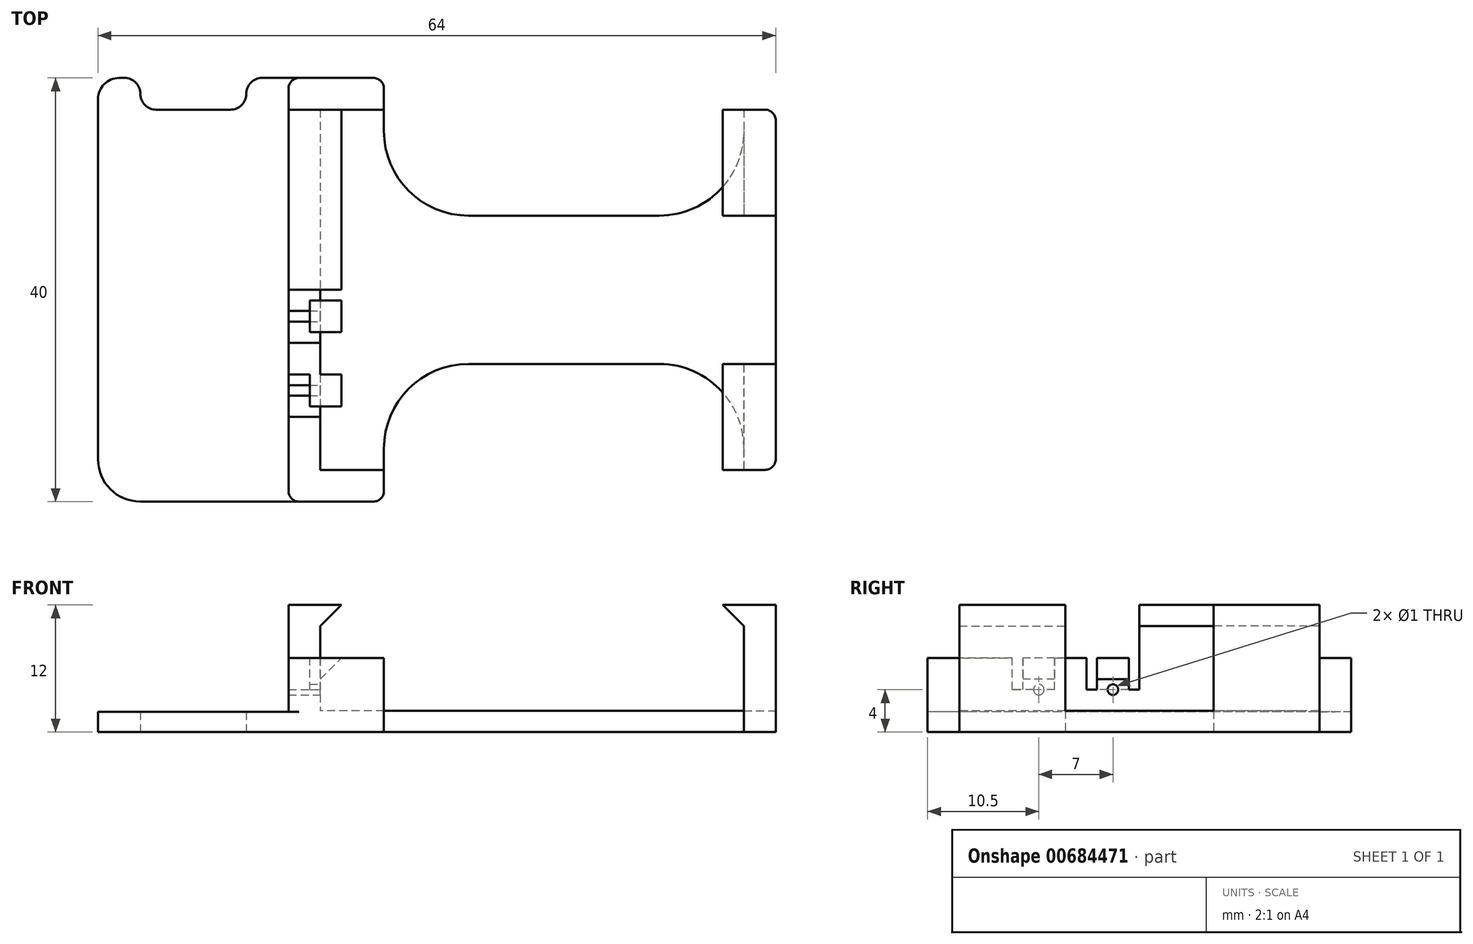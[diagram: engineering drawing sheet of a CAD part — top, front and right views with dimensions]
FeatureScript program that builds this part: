
annotation { "Feature Type Name" : "Feature", "Feature Type Description" : "" }
export const myFeature = defineFeature(function(context is Context, id is Id, definition is map)
    precondition{}
    {
        {
            var Q0;
            Q0=qCreatedBy(makeId("Top.planeOp"),FACE);
            var sketch = newSketch(context, id + "F0", { "sketchPlane" : qUnion([Q0])});
            skLineSegment(sketch, "E0.bottom", {"start": v(20, 17) * mm, "end": v(-20, 17) * mm});
            skLineSegment(sketch, "E0.top", {"start": v(20, -17) * mm, "end": v(-20, -17) * mm});
            skLineSegment(sketch, "E0.left", {"start": v(20, 17) * mm, "end": v(20, -15) * mm});
            skLineSegment(sketch, "E0.right", {"start": v(-20, 17) * mm, "end": v(-20, -17) * mm});
            skPoint(sketch, "E0.middle", {"position": v(0, 0) * mm});
            skLineSegment(sketch, "E1.bottom", {"start": v(20, 17) * mm, "end": v(22, 17) * mm});
            skLineSegment(sketch, "E1.top", {"start": v(20, -17) * mm, "end": v(22, -17) * mm});
            skLineSegment(sketch, "E1.left", {"start": v(20, -15) * mm, "end": v(20, -17) * mm});
            skLineSegment(sketch, "E1.right", {"start": v(23, 16) * mm, "end": v(23, -16) * mm});
            skLineSegment(sketch, "E2.bottom", {"start": v(-20, -17) * mm, "end": v(-23, -17) * mm});
            skLineSegment(sketch, "E2.top", {"start": v(-20, 17) * mm, "end": v(-23, 17) * mm});
            skLineSegment(sketch, "E2.left", {"start": v(-20, -17) * mm, "end": v(-20, -15) * mm});
            skLineSegment(sketch, "E2.right", {"start": v(-23, -17) * mm, "end": v(-23, 17) * mm});
            skLineSegment(sketch, "E3", {"start": v(-12, 7) * mm, "end": v(12, 7) * mm});
            skLineSegment(sketch, "E4", {"start": v(-12, -7) * mm, "end": v(12, -7) * mm});
            skArc(sketch, "E5.filletArc", {"start": v(20, -15) * mm, "mid": v(17.66, -9.34) * mm, "end": v(12, -7) * mm});
            skPoint(sketch, "E6.newPointA", {"position": v(20, -17) * mm});
            skArc(sketch, "E6.filletArc", {"start": v(12, 7) * mm, "mid": v(17.66, 9.34) * mm, "end": v(20, 15) * mm});
            skLineSegment(sketch, "E7", {"start": v(-23, -17) * mm, "end": v(-23, -19) * mm});
            skLineSegment(sketch, "E8", {"start": v(-22, -20) * mm, "end": v(-15, -20) * mm});
            skLineSegment(sketch, "E9", {"start": v(-14, -19) * mm, "end": v(-14, -18) * mm});
            skLineSegment(sketch, "E10", {"start": v(-15, -17) * mm, "end": v(-20, -17) * mm});
            skPoint(sketch, "E11.visualSharp", {"position": v(-14, -20) * mm});
            skArc(sketch, "E11.filletArc", {"start": v(-15, -20) * mm, "mid": v(-14.3, -19.7) * mm, "end": v(-14, -19) * mm});
            skPoint(sketch, "E12.visualSharp", {"position": v(-23, -20) * mm});
            skArc(sketch, "E12.filletArc", {"start": v(-23, -19) * mm, "mid": v(-22.7, -19.7) * mm, "end": v(-22, -20) * mm});
            skLineSegment(sketch, "E13", {"start": v(-23, 17) * mm, "end": v(-23, 19) * mm});
            skLineSegment(sketch, "E14", {"start": v(-22, 20) * mm, "end": v(-15, 20) * mm});
            skLineSegment(sketch, "E15", {"start": v(-14, 19) * mm, "end": v(-14, 18) * mm});
            skLineSegment(sketch, "E16", {"start": v(-15, 17) * mm, "end": v(-23, 17) * mm});
            skPoint(sketch, "E17.visualSharp", {"position": v(-14, 20) * mm});
            skArc(sketch, "E17.filletArc", {"start": v(-14, 19) * mm, "mid": v(-14.3, 19.7) * mm, "end": v(-15, 20) * mm});
            skPoint(sketch, "E18.visualSharp", {"position": v(-23, 20) * mm});
            skArc(sketch, "E18.filletArc", {"start": v(-22, 20) * mm, "mid": v(-22.7, 19.7) * mm, "end": v(-23, 19) * mm});
            skPoint(sketch, "E19.visualSharp", {"position": v(23, 17) * mm});
            skArc(sketch, "E19.filletArc", {"start": v(23, 16) * mm, "mid": v(22.7, 16.7) * mm, "end": v(22, 17) * mm});
            skPoint(sketch, "E20.visualSharp", {"position": v(23, -17) * mm});
            skArc(sketch, "E20.filletArc", {"start": v(22, -17) * mm, "mid": v(22.7, -16.7) * mm, "end": v(23, -16) * mm});
            skPoint(sketch, "E21.visualSharp", {"position": v(-14, -17) * mm});
            skPoint(sketch, "E22.visualSharp", {"position": v(-14, 17) * mm});
            skLineSegment(sketch, "E23", {"start": v(-14, -18) * mm, "end": v(-14, -15) * mm});
            skLineSegment(sketch, "E24", {"start": v(-6, -7) * mm, "end": v(-12, -7) * mm});
            skLineSegment(sketch, "E25", {"start": v(-6, 7) * mm, "end": v(-12, 7) * mm});
            skArc(sketch, "E26.filletArc", {"start": v(-6, -7) * mm, "mid": v(-11.66, -9.34) * mm, "end": v(-14, -15) * mm});
            skLineSegment(sketch, "E27", {"start": v(-14, 15) * mm, "end": v(-14, 18) * mm});
            skPoint(sketch, "E28.visualSharp", {"position": v(-14, 7) * mm});
            skArc(sketch, "E28.filletArc", {"start": v(-14, 15) * mm, "mid": v(-11.66, 9.34) * mm, "end": v(-6, 7) * mm});
            skSolve(sketch);
        }
        {
            var Q0;
            Q0=makeQuery(id+"F0.imprint","IMPRINT",FACE,{"disambiguationData":[TD([[makeQuery(id+"F0.imprint","IMPRINT",EDGE,{"derivedFrom":sQuery(id+"F0.wireOp",EDGE,"E3")}),-1.0]])]});
            var Q1;
            Q1=makeQuery(id+"F0.imprint","IMPRINT",FACE,{"disambiguationData":[TD([[makeQuery(id+"F0.imprint","IMPRINT",EDGE,{"derivedFrom":sQuery(id+"F0.wireOp",EDGE,"E2.bottom")}),-1.0]])]});
            var Q2;
            {var subQ0=sQuery(id+"F0.wireOp",EDGE,"E1.bottom");Q2=makeQuery(id+"F0.imprint","IMPRINT",FACE,{"disambiguationData":[TD([[makeQuery(id+"F0.imprint","IMPRINT",EDGE,{"derivedFrom":subQ0}),-1.0]])]});}
            extrude(context, id + "F1", {"entities" : qUnion([Q0, Q1, Q2]), "depth" : 2 * mm, "offsetDistance" : 25 * mm});
        }
        {
            var Q0;
            Q0=makeQuery(id+"F1.opExtrude","CAP_FACE",FACE,{"disambiguationData":[OSD([sQuery(id+"F0.wireOp",EDGE,"E0.left"),sQuery(id+"F0.wireOp",EDGE,"E0.right"),sQuery(id+"F0.wireOp",EDGE,"E1.bottom"),sQuery(id+"F0.wireOp",EDGE,"E1.top"),sQuery(id+"F0.wireOp",EDGE,"E1.left"),sQuery(id+"F0.wireOp",EDGE,"E1.right"),sQuery(id+"F0.wireOp",EDGE,"E2.bottom"),sQuery(id+"F0.wireOp",EDGE,"E2.top"),sQuery(id+"F0.wireOp",EDGE,"E2.left"),sQuery(id+"F0.wireOp",EDGE,"E2.right"),sQuery(id+"F0.wireOp",EDGE,"E3"),sQuery(id+"F0.wireOp",EDGE,"E4"),sQuery(id+"F0.wireOp",EDGE,"0d2e5045-32be-4d61-923d-7fe529c6475d.filletArc"),sQuery(id+"F0.wireOp",EDGE,"E5.filletArc"),sQuery(id+"F0.wireOp",EDGE,"E6.filletArc"),sQuery(id+"F0.wireOp",EDGE,"e1b89db7-bc73-4bd3-85a6-a36b4de26723.filletArc")])],"isStart":false});
            var sketch = newSketch(context, id + "F2", { "sketchPlane" : qUnion([Q0])});
            skArc(sketch, "E29.0.0", {"start": v(12, -7) * mm, "mid": v(17.66, -9.34) * mm, "end": v(20, -15) * mm});
            skLineSegment(sketch, "E29.0.1", {"start": v(20, -15) * mm, "end": v(20, -17) * mm});
            skLineSegment(sketch, "E29.0.2", {"start": v(20, -17) * mm, "end": v(22, -17) * mm});
            skLineSegment(sketch, "E29.0.3", {"start": v(23, -17) * mm, "end": v(23, 16) * mm});
            skLineSegment(sketch, "E29.0.4", {"start": v(23, 17) * mm, "end": v(20, 17) * mm});
            skLineSegment(sketch, "E29.0.5", {"start": v(20, 15) * mm, "end": v(20, -17) * mm});
            skArc(sketch, "E29.0.6", {"start": v(20, 15) * mm, "mid": v(17.66, 9.34) * mm, "end": v(12, 7) * mm});
            skLineSegment(sketch, "E29.0.7", {"start": v(12, 7) * mm, "end": v(-6, 7) * mm});
            skArc(sketch, "E29.0.8", {"start": v(-6, 7) * mm, "mid": v(-11.66, 9.34) * mm, "end": v(-14, 15) * mm});
            skLineSegment(sketch, "E29.0.10", {"start": v(-14, 17) * mm, "end": v(-23, 17) * mm});
            skLineSegment(sketch, "E29.0.11", {"start": v(-23, 17) * mm, "end": v(-23, -17) * mm});
            skLineSegment(sketch, "E29.0.12", {"start": v(-23, -17) * mm, "end": v(-14, -17) * mm});
            skLineSegment(sketch, "E29.0.13", {"start": v(-14, -17) * mm, "end": v(-14, -15) * mm});
            skLineSegment(sketch, "E29.0.15", {"start": v(-12, -7) * mm, "end": v(12, -7) * mm});
            skLineSegment(sketch, "E30", {"start": v(20, -7) * mm, "end": v(23, -7) * mm});
            skLineSegment(sketch, "E31", {"start": v(20, 7) * mm, "end": v(23, 7) * mm});
            skLineSegment(sketch, "E32", {"start": v(-14, -7) * mm, "end": v(-23, -7) * mm});
            skLineSegment(sketch, "E33", {"start": v(-23, 0) * mm, "end": v(-14, 0) * mm});
            skLineSegment(sketch, "E34", {"start": v(-20, 17) * mm, "end": v(-20, -17) * mm});
            skSolve(sketch);
        }
        {
            var Q0;
            {var subQ1=sQuery(id+"F2.wireOp",EDGE,"E29.0.10");Q0=makeQuery(id+"F2.imprint","IMPRINT",FACE,{"disambiguationData":[TD([[makeQuery(id+"F2.imprint","IMPRINT",EDGE,{"derivedFrom":subQ1}),1.0]])]});}
            var Q1;
            {var subQ3=sQuery(id+"F2.wireOp",EDGE,"E29.0.2");Q1=makeQuery(id+"F2.imprint","IMPRINT",FACE,{"disambiguationData":[TD([[makeQuery(id+"F2.imprint","IMPRINT",EDGE,{"derivedFrom":subQ3}),1.0]])]});}
            var Q2;
            {var subQ3=sQuery(id+"F2.wireOp",EDGE,"E29.0.4");Q2=makeQuery(id+"F2.imprint","IMPRINT",FACE,{"disambiguationData":[TD([[makeQuery(id+"F2.imprint","IMPRINT",EDGE,{"derivedFrom":subQ3}),-1.0]])]});}
            var Q3;
            {var subQ0=sQuery(id+"F2.wireOp",EDGE,"SwYouN3J-6pRH-B4eC-V0e7-ENGrIOtCNmfV");Q3=makeQuery(id+"F2.imprint","IMPRINT",FACE,{"disambiguationData":[TD([[makeQuery(id+"F2.imprint","IMPRINT",EDGE,{"derivedFrom":subQ0}),1.0]])]});}
            extrude(context, id + "F3", {"entities" : qUnion([Q0, Q1, Q2, Q3]), "operationType" : NewBodyOperationType.ADD, "depth" : 10 * mm, "offsetDistance" : 25 * mm});
        }
        {
            var Q0;
            Q0=makeQuery(id+"F3.boolean.opBoolean","MERGE",FACE,{"derivedFrom":[makeQuery(id+"F1.opExtrude","SWEPT_FACE",FACE,{"disambiguationData":[OSD([sQuery(id+"F0.wireOp",EDGE,"E1.left")])]}),makeQuery(id+"F3.opExtrude","SWEPT_FACE",FACE,{"disambiguationData":[OSD([sQuery(id+"F2.wireOp",EDGE,"E29.0.5")])]})]});
            var sketch = newSketch(context, id + "F4", { "sketchPlane" : qUnion([Q0])});
            skLineSegment(sketch, "E35.bottom", {"start": v(-17, 12) * mm, "end": v(-7, 12) * mm});
            skLineSegment(sketch, "E35.top", {"start": v(-17, 10) * mm, "end": v(-7, 10) * mm});
            skLineSegment(sketch, "E35.left", {"start": v(-17, 12) * mm, "end": v(-17, 10) * mm});
            skLineSegment(sketch, "E35.right", {"start": v(-7, 12) * mm, "end": v(-7, 10) * mm});
            skLineSegment(sketch, "E36.0.0", {"start": v(15, 0) * mm, "end": v(17, 0) * mm});
            skLineSegment(sketch, "E36.0.1", {"start": v(17, 0) * mm, "end": v(17, 12) * mm});
            skLineSegment(sketch, "E36.0.2", {"start": v(17, 12) * mm, "end": v(7, 12) * mm});
            skLineSegment(sketch, "E36.0.3", {"start": v(7, 12) * mm, "end": v(7, 2) * mm});
            skLineSegment(sketch, "E36.0.4", {"start": v(7, 2) * mm, "end": v(15, 2) * mm});
            skLineSegment(sketch, "E36.0.5", {"start": v(15, 2) * mm, "end": v(15, 0) * mm});
            skLineSegment(sketch, "E37.0.0", {"start": v(-15, 0) * mm, "end": v(-17, 0) * mm});
            skLineSegment(sketch, "E37.0.1", {"start": v(-17, 0) * mm, "end": v(-17, 12) * mm});
            skLineSegment(sketch, "E37.0.2", {"start": v(-17, 12) * mm, "end": v(17, 12) * mm});
            skLineSegment(sketch, "E37.0.3", {"start": v(17, 12) * mm, "end": v(17, 0) * mm});
            skLineSegment(sketch, "E37.0.4", {"start": v(17, 0) * mm, "end": v(15, 0) * mm});
            skLineSegment(sketch, "E37.0.5", {"start": v(15, 0) * mm, "end": v(15, 2) * mm});
            skLineSegment(sketch, "E37.0.6", {"start": v(15, 2) * mm, "end": v(-15, 2) * mm});
            skLineSegment(sketch, "E37.0.7", {"start": v(-15, 2) * mm, "end": v(-15, 0) * mm});
            skLineSegment(sketch, "E38.top", {"start": v(17, 10) * mm, "end": v(7, 10) * mm});
            skLineSegment(sketch, "E38.left", {"start": v(17, 12) * mm, "end": v(17, 10) * mm});
            skLineSegment(sketch, "E38.right", {"start": v(7, 12) * mm, "end": v(7, 10) * mm});
            skSolve(sketch);
        }
        {
            var Q0;
            {var subQ0=sQuery(id+"F4.wireOp",EDGE,"E35.top");Q0=makeQuery(id+"F4.imprint","IMPRINT",FACE,{"disambiguationData":[TD([[makeQuery(id+"F4.imprint","IMPRINT",EDGE,{"derivedFrom":subQ0}),1.0]])]});}
            var Q1;
            Q1=makeQuery(id+"F4.imprint","IMPRINT",FACE,{"disambiguationData":[TD([[makeQuery(id+"F4.imprint","IMPRINT",EDGE,{"derivedFrom":sQuery(id+"F4.wireOp",EDGE,"E36.0.2")}),-1.0]])]});
            extrude(context, id + "F5", {"entities" : qUnion([Q0, Q1]), "operationType" : NewBodyOperationType.ADD, "depth" : 2 * mm, "offsetDistance" : 25 * mm});
        }
        {
            var Q0;
            Q0=makeQuery(id+"F5.opExtrude","CAP_EDGE",EDGE,{"disambiguationData":[OSD([sQuery(id+"F4.wireOp",EDGE,"E35.top")])],"isStart":false});
            var Q1;
            Q1=makeQuery(id+"F5.opExtrude","CAP_EDGE",EDGE,{"disambiguationData":[OSD([sQuery(id+"F4.wireOp",EDGE,"E38.top")])],"isStart":false});
            chamfer(context, id + "F6", {"entities" : qUnion([Q0, Q1]), "width" : 2 * mm, "tangentPropagation" : true});
        }
        {
            var Q0;
            {var subQ0=sQuery(id+"F2.wireOp",EDGE,"E29.0.12");Q0=makeQuery(id+"F2.imprint","IMPRINT",FACE,{"disambiguationData":[TD([[makeQuery(id+"F2.imprint","IMPRINT",EDGE,{"derivedFrom":subQ0}),-1.0]])]});}
            var Q1;
            {var subQ0=sQuery(id+"F2.wireOp",EDGE,"E32");Q1=makeQuery(id+"F2.imprint","IMPRINT",FACE,{"disambiguationData":[TD([[makeQuery(id+"F2.imprint","IMPRINT",EDGE,{"derivedFrom":subQ0}),-1.0]])]});}
            extrude(context, id + "F7", {"entities" : qUnion([Q0, Q1]), "operationType" : NewBodyOperationType.ADD, "depth" : 5 * mm, "offsetDistance" : 25 * mm});
        }
        {
            var Q0;
            Q0=makeQuery(id+"F0.imprint","IMPRINT",FACE,{"disambiguationData":[TD([[makeQuery(id+"F0.imprint","IMPRINT",EDGE,{"derivedFrom":sQuery(id+"F0.wireOp",EDGE,"E2.bottom")}),1.0]])]});
            var Q1;
            {var subQ3=sQuery(id+"F0.wireOp",EDGE,"E13");Q1=makeQuery(id+"F0.imprint","IMPRINT",FACE,{"disambiguationData":[TD([[makeQuery(id+"F0.imprint","IMPRINT",EDGE,{"derivedFrom":subQ3}),-1.0]])]});}
            extrude(context, id + "F8", {"entities" : qUnion([Q0, Q1]), "operationType" : NewBodyOperationType.ADD, "depth" : 7 * mm, "offsetDistance" : 25 * mm});
        }
        {
            var Q0;
            {var subQ0=sQuery(id+"F2.wireOp",EDGE,"E34");Q0=makeQuery(id+"F7.boolean.opBoolean","MERGE",FACE,{"derivedFrom":[makeQuery(id+"F3.opExtrude","SWEPT_FACE",FACE,{"disambiguationData":[OSD([subQ0])]}),makeQuery(id+"F7.opExtrude","SWEPT_FACE",FACE,{"disambiguationData":[OSD([subQ0])]})]});}
            var sketch = newSketch(context, id + "F9", { "sketchPlane" : qUnion([Q0])});
            skLineSegment(sketch, "E39.bottom", {"start": v(17, 12) * mm, "end": v(0, 12) * mm});
            skLineSegment(sketch, "E39.top", {"start": v(17, 10) * mm, "end": v(0, 10) * mm});
            skLineSegment(sketch, "E39.left", {"start": v(17, 12) * mm, "end": v(17, 10) * mm});
            skLineSegment(sketch, "E39.right", {"start": v(0, 12) * mm, "end": v(0, 10) * mm});
            skSolve(sketch);
        }
        {
            var Q0;
            Q0=makeQuery(id+"F9.imprint","IMPRINT",FACE,{"disambiguationData":[TD([[makeQuery(id+"F9.imprint","IMPRINT",EDGE,{"derivedFrom":sQuery(id+"F9.wireOp",EDGE,"E39.bottom")}),1.0]])]});
            extrude(context, id + "F10", {"entities" : qUnion([Q0]), "operationType" : NewBodyOperationType.ADD, "depth" : 2 * mm, "offsetDistance" : 25 * mm});
        }
        {
            var Q0;
            Q0=makeQuery(id+"F10.opExtrude","CAP_EDGE",EDGE,{"disambiguationData":[OSD([sQuery(id+"F9.wireOp",EDGE,"E39.top")])],"isStart":false});
            chamfer(context, id + "F11", {"entities" : qUnion([Q0]), "width" : 2 * mm, "tangentPropagation" : true});
        }
        {
            var Q0;
            Q0=makeQuery(id+"F8.boolean.opBoolean","MERGE",FACE,{"derivedFrom":[makeQuery(id+"F7.opExtrude","CAP_FACE",FACE,{"disambiguationData":[OSD([sQuery(id+"F2.wireOp",EDGE,"E29.0.11"),sQuery(id+"F2.wireOp",EDGE,"E29.0.12"),sQuery(id+"F2.wireOp",EDGE,"E33"),sQuery(id+"F2.wireOp",EDGE,"E34")])],"isStart":false}),makeQuery(id+"F8.opExtrude","CAP_FACE",FACE,{"disambiguationData":[OSD([sQuery(id+"F0.wireOp",EDGE,"E0.top"),sQuery(id+"F0.wireOp",EDGE,"E2.bottom"),sQuery(id+"F0.wireOp",EDGE,"E7"),sQuery(id+"F0.wireOp",EDGE,"E8"),sQuery(id+"F0.wireOp",EDGE,"E9"),sQuery(id+"F0.wireOp",EDGE,"E10"),sQuery(id+"F0.wireOp",EDGE,"E11.filletArc"),sQuery(id+"F0.wireOp",EDGE,"E12.filletArc"),sQuery(id+"F0.wireOp",EDGE,"E23")])],"isStart":false})]});
            var sketch = newSketch(context, id + "F12", { "sketchPlane" : qUnion([Q0])});
            skLineSegment(sketch, "E40", {"start": v(-20, -17) * mm, "end": v(-20, -9.5) * mm});
            skLineSegment(sketch, "E41", {"start": v(-20, -9.5) * mm, "end": v(-19.15, -9.5) * mm});
            skLineSegment(sketch, "E42", {"start": v(-20, -2.5) * mm, "end": v(-17.2, -2.5) * mm});
            skLineSegment(sketch, "E43.bottom", {"start": v(-23, -8) * mm, "end": v(-17, -8) * mm});
            skLineSegment(sketch, "E43.top", {"start": v(-23, -11) * mm, "end": v(-17, -11) * mm});
            skLineSegment(sketch, "E43.left", {"start": v(-23, -8) * mm, "end": v(-23, -11) * mm});
            skLineSegment(sketch, "E43.right", {"start": v(-17, -8) * mm, "end": v(-17, -11) * mm});
            skPoint(sketch, "E43.middle", {"position": v(-20, -9.5) * mm});
            skLineSegment(sketch, "E44.bottom", {"start": v(-23, -1) * mm, "end": v(-17, -1) * mm});
            skLineSegment(sketch, "E44.top", {"start": v(-23, -4) * mm, "end": v(-17, -4) * mm});
            skLineSegment(sketch, "E44.left", {"start": v(-23, -1) * mm, "end": v(-23, -4) * mm});
            skLineSegment(sketch, "E44.right", {"start": v(-17, -1) * mm, "end": v(-17, -4) * mm});
            skPoint(sketch, "E44.middle", {"position": v(-20, -2.5) * mm});
            skSolve(sketch);
        }
        {
            var Q0;
            {var subQ0=sQuery(id+"F2.wireOp",EDGE,"E34");Q0=makeQuery(id+"F7.boolean.opBoolean","MERGE",FACE,{"derivedFrom":[makeQuery(id+"F3.opExtrude","SWEPT_FACE",FACE,{"disambiguationData":[OSD([subQ0])]}),makeQuery(id+"F7.opExtrude","SWEPT_FACE",FACE,{"disambiguationData":[OSD([subQ0])]})]});}
            var sketch = newSketch(context, id + "F13", { "sketchPlane" : qUnion([Q0])});
            skLineSegment(sketch, "E45", {"start": v(-17, 7) * mm, "end": v(-9.5, 7) * mm});
            skLineSegment(sketch, "E46", {"start": v(-9.5, 7) * mm, "end": v(-9.5, 6) * mm});
            skLineSegment(sketch, "E47", {"start": v(-2.5, 7) * mm, "end": v(-2.5, 6) * mm});
            skLineSegment(sketch, "E48.bottom", {"start": v(-8, 7) * mm, "end": v(-11, 7) * mm});
            skLineSegment(sketch, "E48.top", {"start": v(-8, 5) * mm, "end": v(-11, 5) * mm});
            skLineSegment(sketch, "E48.left", {"start": v(-8, 7) * mm, "end": v(-8, 5) * mm});
            skLineSegment(sketch, "E48.right", {"start": v(-11, 7) * mm, "end": v(-11, 5) * mm});
            skPoint(sketch, "E48.middle", {"position": v(-9.5, 6) * mm});
            skLineSegment(sketch, "E49.bottom", {"start": v(-1, 7) * mm, "end": v(-4, 7) * mm});
            skLineSegment(sketch, "E49.top", {"start": v(-1, 5) * mm, "end": v(-4, 5) * mm});
            skLineSegment(sketch, "E49.left", {"start": v(-1, 7) * mm, "end": v(-1, 5) * mm});
            skLineSegment(sketch, "E49.right", {"start": v(-4, 7) * mm, "end": v(-4, 5) * mm});
            skPoint(sketch, "E49.middle", {"position": v(-2.5, 6) * mm});
            skSolve(sketch);
        }
        {
            var Q0;
            Q0 = qSketchRegion(id + "F13", true);
            extrude(context, id + "F14", {"entities" : qUnion([Q0]), "operationType" : NewBodyOperationType.ADD, "depth" : 2 * mm, "offsetDistance" : 25 * mm});
        }
        {
            var Q0;
            Q0=makeQuery(id+"F14.opExtrude","CAP_EDGE",EDGE,{"disambiguationData":[OSD([sQuery(id+"F13.wireOp",EDGE,"E48.top")])],"isStart":false});
            var Q1;
            Q1=makeQuery(id+"F14.opExtrude","CAP_EDGE",EDGE,{"disambiguationData":[OSD([sQuery(id+"F13.wireOp",EDGE,"E49.top")])],"isStart":false});
            chamfer(context, id + "F15", {"entities" : qUnion([Q0, Q1]), "width" : 2 * mm, "tangentPropagation" : true});
        }
        {
            var Q0;
            {var subQ0=sQuery(id+"F12.wireOp",EDGE,"E43.bottom");var subQ3=makeQuery(id+"F7.opExtrude","CAP_EDGE",EDGE,{"disambiguationData":[OSD([sQuery(id+"F2.wireOp",EDGE,"E34")])],"isStart":false});var subQ4=makeQuery(id+"F12.imprint","INTERSECT",VERTEX,{"derivedFrom":[subQ3,subQ0]});Q0=makeQuery(id+"F12.imprint","IMPRINT",FACE,{"disambiguationData":[TD([[makeQuery(id+"F12.imprint","IMPRINT",EDGE,{"disambiguationData":[TD([[subQ4,1.0]])],"derivedFrom":subQ3}),-1.0]])]});}
            var sketch = newSketch(context, id + "F16", { "sketchPlane" : qUnion([Q0])});
            skLineSegment(sketch, "E50.0.0", {"start": v(-23, -1) * mm, "end": v(-23, -4) * mm});
            skLineSegment(sketch, "E50.0.1", {"start": v(-21, -4) * mm, "end": v(-20, -4) * mm});
            skLineSegment(sketch, "E50.0.2", {"start": v(-20, -4) * mm, "end": v(-20, -2.5) * mm});
            skLineSegment(sketch, "E50.0.3", {"start": v(-20, -2.5) * mm, "end": v(-20, -1) * mm});
            skLineSegment(sketch, "E50.0.4", {"start": v(-20, -1) * mm, "end": v(-21, -1) * mm});
            skLineSegment(sketch, "E51.0.0", {"start": v(-23, -8) * mm, "end": v(-23, -11) * mm});
            skLineSegment(sketch, "E51.0.1", {"start": v(-21, -11) * mm, "end": v(-20, -11) * mm});
            skLineSegment(sketch, "E51.0.2", {"start": v(-20, -11) * mm, "end": v(-20, -9.5) * mm});
            skLineSegment(sketch, "E51.0.3", {"start": v(-20, -9.5) * mm, "end": v(-20, -8) * mm});
            skLineSegment(sketch, "E51.0.4", {"start": v(-20, -8) * mm, "end": v(-21, -8) * mm});
            skLineSegment(sketch, "E52", {"start": v(-21, -1) * mm, "end": v(-21, -4) * mm});
            skLineSegment(sketch, "E53", {"start": v(-21, -8) * mm, "end": v(-21, -11) * mm});
            skLineSegment(sketch, "E54.0", {"start": v(-20, -17) * mm, "end": v(-20, -9.5) * mm});
            skLineSegment(sketch, "E55.0", {"start": v(-20, -4) * mm, "end": v(-20, -8) * mm});
            skLineSegment(sketch, "E56.0", {"start": v(-20, 0) * mm, "end": v(-20, -1) * mm});
            skLineSegment(sketch, "E57", {"start": v(-20, -12) * mm, "end": v(-21, -12) * mm});
            skLineSegment(sketch, "E58", {"start": v(-21, -7) * mm, "end": v(-20, -7) * mm});
            skLineSegment(sketch, "E59", {"start": v(-21, -7) * mm, "end": v(-23, -7) * mm});
            skLineSegment(sketch, "E60", {"start": v(-23, -7) * mm, "end": v(-23, -8) * mm});
            skLineSegment(sketch, "E61", {"start": v(-23, -11) * mm, "end": v(-23, -12) * mm});
            skLineSegment(sketch, "E62", {"start": v(-23, -12) * mm, "end": v(-21, -12) * mm});
            skLineSegment(sketch, "E63", {"start": v(-20, -5) * mm, "end": v(-23, -5) * mm});
            skLineSegment(sketch, "E64", {"start": v(-23, -5) * mm, "end": v(-23, -4) * mm});
            skLineSegment(sketch, "E65", {"start": v(-20, 0) * mm, "end": v(-23, 0) * mm});
            skLineSegment(sketch, "E66", {"start": v(-23, 0) * mm, "end": v(-23, -1) * mm});
            skLineSegment(sketch, "E67", {"start": v(-20, -5) * mm, "end": v(-20, -4) * mm});
            skLineSegment(sketch, "E68", {"start": v(-21, -4) * mm, "end": v(-21, -1) * mm});
            skLineSegment(sketch, "E69", {"start": v(-20, -1) * mm, "end": v(-20, 0) * mm});
            skLineSegment(sketch, "E70", {"start": v(-23, 0) * mm, "end": v(-23, -5) * mm});
            skLineSegment(sketch, "E71", {"start": v(-23, -8) * mm, "end": v(-23, -7) * mm});
            skLineSegment(sketch, "E72", {"start": v(-20, -7) * mm, "end": v(-23, -7) * mm});
            skLineSegment(sketch, "E73", {"start": v(-20, -7) * mm, "end": v(-20, -8) * mm});
            skSolve(sketch);
        }
        {
            var Q0;
            Q0=makeQuery(id+"F16.imprint","IMPRINT",FACE,{"disambiguationData":[TD([[makeQuery(id+"F16.imprint","IMPRINT",EDGE,{"derivedFrom":sQuery(id+"F16.wireOp",EDGE,"E50.0.4")}),-1.0]])]});
            var Q1;
            {var subQ7=sQuery(id+"F16.wireOp",EDGE,"E50.0.1");Q1=makeQuery(id+"F16.imprint","IMPRINT",FACE,{"disambiguationData":[TD([[makeQuery(id+"F16.imprint","IMPRINT",EDGE,{"derivedFrom":subQ7}),-1.0]])]});}
            var Q2;
            {var subQ4=sQuery(id+"F16.wireOp",EDGE,"E51.0.0");Q2=makeQuery(id+"F16.imprint","IMPRINT",FACE,{"disambiguationData":[TD([[makeQuery(id+"F16.imprint","IMPRINT",EDGE,{"derivedFrom":subQ4}),1.0]])]});}
            var Q3;
            {var subQ1=sQuery(id+"F16.wireOp",EDGE,"E71");Q3=makeQuery(id+"F16.imprint","IMPRINT",FACE,{"disambiguationData":[TD([[makeQuery(id+"F16.imprint","IMPRINT",EDGE,{"derivedFrom":subQ1}),-1.0]])]});}
            extrude(context, id + "F17", {"entities" : qUnion([Q0, Q1, Q2, Q3]), "operationType" : NewBodyOperationType.REMOVE, "oppositeDirection" : true, "depth" : 3 * mm, "offsetDistance" : 25 * mm});
        }
        {
            var Q0;
            {var subQ0=sQuery(id+"F2.wireOp",EDGE,"E34");Q0=makeQuery(id+"F7.boolean.opBoolean","MERGE",FACE,{"derivedFrom":[makeQuery(id+"F3.opExtrude","SWEPT_FACE",FACE,{"disambiguationData":[OSD([subQ0])]}),makeQuery(id+"F7.opExtrude","SWEPT_FACE",FACE,{"disambiguationData":[OSD([subQ0])]})]});}
            var sketch = newSketch(context, id + "F18", { "sketchPlane" : qUnion([Q0])});
            skCircle(sketch, "E74", {"center": v(-9.5, 4) * mm, "radius": 0.5 * mm});
            skPoint(sketch, "E74.centerSnap0", {"position": v(-9.5, 5) * mm});
            skCircle(sketch, "E75", {"center": v(-2.5, 4) * mm, "radius": 0.5 * mm});
            skPoint(sketch, "E75.centerSnap0", {"position": v(-2.5, 5) * mm});
            skSolve(sketch);
        }
        {
            var Q0;
            Q0=makeQuery(id+"F18.imprint","IMPRINT",FACE,{"disambiguationData":[TD([[makeQuery(id+"F18.imprint","IMPRINT",EDGE,{"derivedFrom":sQuery(id+"F18.wireOp",EDGE,"E74")}),1.0]])]});
            var Q1;
            Q1=makeQuery(id+"F18.imprint","IMPRINT",FACE,{"disambiguationData":[TD([[makeQuery(id+"F18.imprint","IMPRINT",EDGE,{"derivedFrom":sQuery(id+"F18.wireOp",EDGE,"E75")}),1.0]])]});
            extrude(context, id + "F19", {"entities" : qUnion([Q0, Q1]), "operationType" : NewBodyOperationType.REMOVE, "endBound" : BoundingType.THROUGH_ALL, "oppositeDirection" : true, "depth" : 25 * mm, "offsetDistance" : 25 * mm});
        }
        {
            var Q0;
            Q0=qCreatedBy(makeId("Top.planeOp"),FACE);
            var sketch = newSketch(context, id + "F20", { "sketchPlane" : qUnion([Q0])});
            skLineSegment(sketch, "E76.0", {"start": v(-23, -17) * mm, "end": v(-23, 17) * mm});
            skPoint(sketch, "E77.0", {"position": v(-23, 18) * mm});
            skPoint(sketch, "E78.0", {"position": v(-23, 20) * mm});
            skPoint(sketch, "E79.0", {"position": v(-23, -20) * mm});
            skLineSegment(sketch, "E80.bottom", {"start": v(-23, 20) * mm, "end": v(-25.5, 20) * mm});
            skLineSegment(sketch, "E80.top", {"start": v(-23, -20) * mm, "end": v(-37, -20) * mm});
            skLineSegment(sketch, "E80.left", {"start": v(-23, 20) * mm, "end": v(-23, -20) * mm});
            skLineSegment(sketch, "E80.right", {"start": v(-41, 16) * mm, "end": v(-41, -16) * mm});
            skArc(sketch, "E81.0", {"start": v(-22, 20) * mm, "mid": v(-22.7, 19.7) * mm, "end": v(-23, 19) * mm});
            skArc(sketch, "E82.0", {"start": v(-23, -19) * mm, "mid": v(-22.7, -19.7) * mm, "end": v(-22, -20) * mm});
            skPoint(sketch, "E83.0", {"position": v(-23, -18) * mm});
            skLineSegment(sketch, "E84.0", {"start": v(-23, -17) * mm, "end": v(-23, -19) * mm});
            skLineSegment(sketch, "E85", {"start": v(-23, 20) * mm, "end": v(-22, 20) * mm});
            skLineSegment(sketch, "E86", {"start": v(-22, -20) * mm, "end": v(-23, -20) * mm});
            skPoint(sketch, "E87.visualSharp", {"position": v(-41, 20) * mm});
            skPoint(sketch, "E88.visualSharp", {"position": v(-41, -20) * mm});
            skArc(sketch, "E88.filletArc", {"start": v(-41, -16) * mm, "mid": v(-39.83, -18.83) * mm, "end": v(-37, -20) * mm});
            skLineSegment(sketch, "E89", {"start": v(-39, 20) * mm, "end": v(-38.5, 20) * mm});
            skLineSegment(sketch, "E90.bottom", {"start": v(-28.5, 17) * mm, "end": v(-35.5, 17) * mm});
            skLineSegment(sketch, "E90.left", {"start": v(-27, 18.5) * mm, "end": v(-27, 18.5) * mm});
            skLineSegment(sketch, "E90.right", {"start": v(-37, 18.5) * mm, "end": v(-37, 18.5) * mm});
            skPoint(sketch, "E90.middle", {"position": v(-32, 20) * mm});
            skPoint(sketch, "E91.orphan", {"position": v(-27, 23) * mm});
            skPoint(sketch, "E92.orphan", {"position": v(-37, 23) * mm});
            skLineSegment(sketch, "E93", {"start": v(-41, 18) * mm, "end": v(-41, 16) * mm});
            skArc(sketch, "E94.filletArc", {"start": v(-39, 20) * mm, "mid": v(-40.41, 19.41) * mm, "end": v(-41, 18) * mm});
            skPoint(sketch, "E95.visualSharp", {"position": v(-27, 20) * mm});
            skArc(sketch, "E95.filletArc", {"start": v(-25.5, 20) * mm, "mid": v(-26.56, 19.56) * mm, "end": v(-27, 18.5) * mm});
            skPoint(sketch, "E96.visualSharp", {"position": v(-37, 17) * mm});
            skArc(sketch, "E96.filletArc", {"start": v(-37, 18.5) * mm, "mid": v(-36.56, 17.44) * mm, "end": v(-35.5, 17) * mm});
            skPoint(sketch, "E97.visualSharp", {"position": v(-27, 17) * mm});
            skArc(sketch, "E97.filletArc", {"start": v(-28.5, 17) * mm, "mid": v(-27.44, 17.44) * mm, "end": v(-27, 18.5) * mm});
            skPoint(sketch, "E98.visualSharp", {"position": v(-37, 20) * mm});
            skArc(sketch, "E98.filletArc", {"start": v(-37, 18.5) * mm, "mid": v(-37.44, 19.56) * mm, "end": v(-38.5, 20) * mm});
            skSolve(sketch);
        }
        {
            var Q0;
            {var subQ0=sQuery(id+"F20.wireOp",EDGE,"E80.bottom");Q0=makeQuery(id+"F20.imprint","IMPRINT",FACE,{"disambiguationData":[TD([[makeQuery(id+"F20.imprint","IMPRINT",EDGE,{"derivedFrom":subQ0}),1.0]])]});}
            var Q1;
            {var subQ2=sQuery(id+"F20.wireOp",EDGE,"E81.0");Q1=makeQuery(id+"F20.imprint","IMPRINT",FACE,{"disambiguationData":[TD([[makeQuery(id+"F20.imprint","IMPRINT",EDGE,{"derivedFrom":subQ2}),-1.0]])]});}
            var Q2;
            {var subQ2=sQuery(id+"F20.wireOp",EDGE,"E82.0");Q2=makeQuery(id+"F20.imprint","IMPRINT",FACE,{"disambiguationData":[TD([[makeQuery(id+"F20.imprint","IMPRINT",EDGE,{"derivedFrom":subQ2}),-1.0]])]});}
            extrude(context, id + "F21", {"entities" : qUnion([Q0, Q1, Q2]), "operationType" : NewBodyOperationType.ADD, "depth" : 1.9 * mm, "offsetDistance" : 25 * mm});
        }
    });
